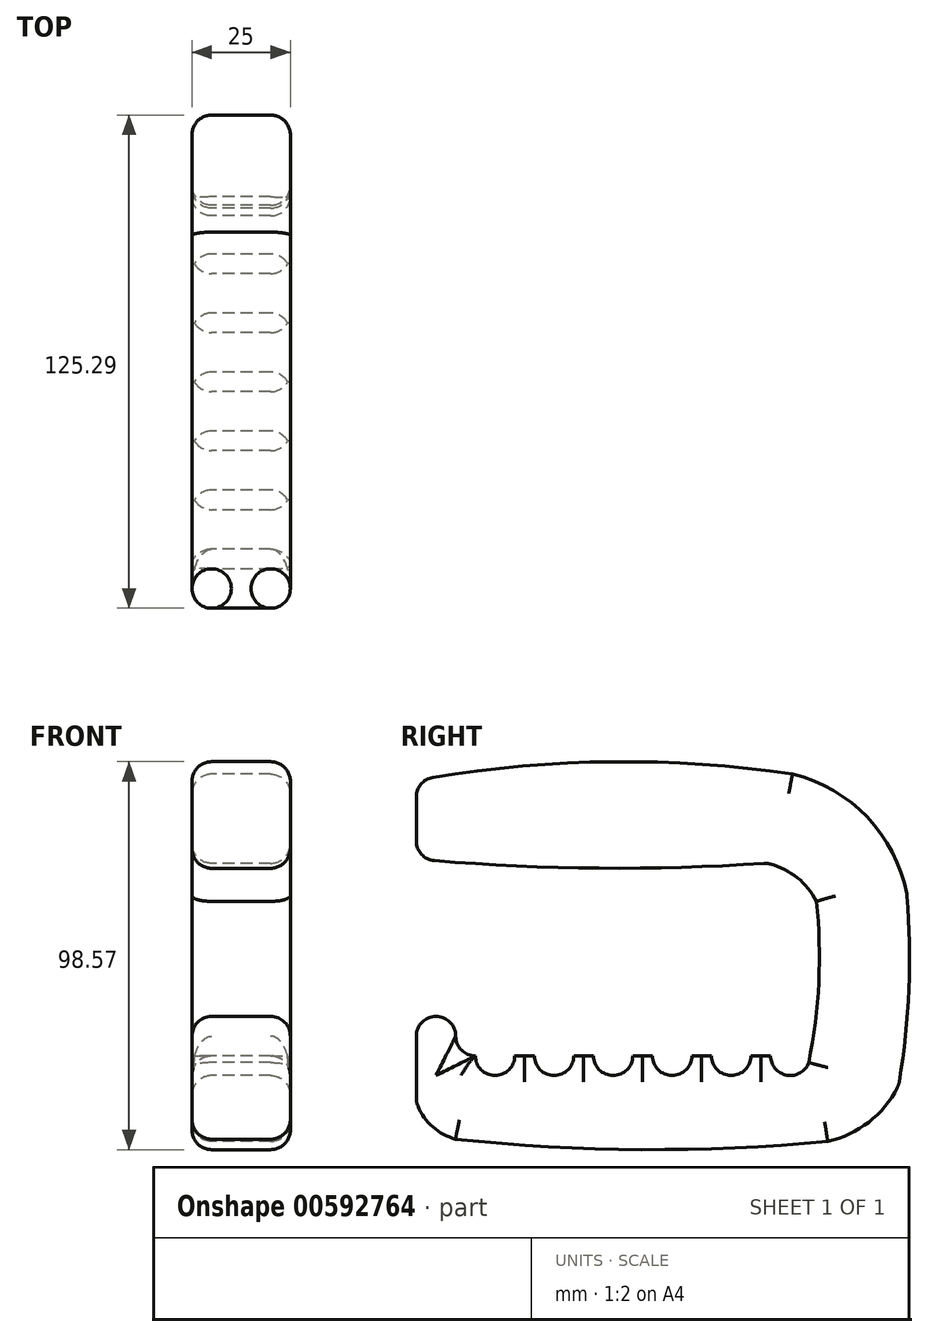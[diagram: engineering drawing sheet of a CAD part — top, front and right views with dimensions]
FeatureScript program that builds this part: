
annotation { "Feature Type Name" : "Feature", "Feature Type Description" : "" }
export const myFeature = defineFeature(function(context is Context, id is Id, definition is map)
    precondition{}
    {
        {
            var Q0;
            Q0=qCreatedBy(makeId("Right.planeOp"),FACE);
            var sketch = newSketch(context, id + "F0", { "sketchPlane" : qUnion([Q0])});
            skLineSegment(sketch, "E0", {"start": v(0, 0) * mm, "end": v(0, 90) * mm, "construction": true});
            skLineSegment(sketch, "E1", {"start": v(-120, 90) * mm, "end": v(-120, 70) * mm});
            skLineSegment(sketch, "E2", {"start": v(-120, 8.28) * mm, "end": v(-120, 30) * mm});
            skLineSegment(sketch, "E3", {"start": v(-120, 30) * mm, "end": v(-110, 30) * mm});
            skLineSegment(sketch, "E4", {"start": v(-110, 30) * mm, "end": v(-110, 20) * mm});
            skPoint(sketch, "E5.orphan", {"position": v(-120, 20) * mm});
            skLineSegment(sketch, "E6", {"start": v(-110, 20) * mm, "end": v(-105, 20) * mm});
            skArc(sketch, "E7", {"start": v(-105, 20) * mm, "mid": v(-100, 15) * mm, "end": v(-95, 20) * mm});
            skLineSegment(sketch, "E8", {"start": v(-95, 20) * mm, "end": v(-90, 20) * mm});
            skArc(sketch, "E9", {"start": v(-90, 20) * mm, "mid": v(-85, 15) * mm, "end": v(-80, 20) * mm});
            skLineSegment(sketch, "E10", {"start": v(-80, 20) * mm, "end": v(-75, 20) * mm});
            skArc(sketch, "E11", {"start": v(-75, 20) * mm, "mid": v(-70, 15) * mm, "end": v(-65, 20) * mm});
            skLineSegment(sketch, "E12", {"start": v(-65, 20) * mm, "end": v(-60, 20) * mm});
            skArc(sketch, "E13", {"start": v(-60, 20) * mm, "mid": v(-55, 15) * mm, "end": v(-50, 20) * mm});
            skLineSegment(sketch, "E14", {"start": v(-50, 20) * mm, "end": v(-45, 20) * mm});
            skArc(sketch, "E15", {"start": v(-45, 20) * mm, "mid": v(-40, 15) * mm, "end": v(-35, 20) * mm});
            skLineSegment(sketch, "E16", {"start": v(-35, 20) * mm, "end": v(-30, 20) * mm});
            skArc(sketch, "E17", {"start": v(-30, 20) * mm, "mid": v(-25.86, 15.08) * mm, "end": v(-20.3, 18.3) * mm});
            skArc(sketch, "E18", {"start": v(2.59, 12.74) * mm, "mid": v(5.11, 36.72) * mm, "end": v(4.64, 60.83) * mm});
            skArc(sketch, "E19", {"start": v(-120, 70) * mm, "mid": v(-75.5, 67.7) * mm, "end": v(-30.96, 68.94) * mm});
            skPoint(sketch, "E20.orphan", {"position": v(-17.66, 70) * mm});
            skArc(sketch, "E21", {"start": v(-110.03, -1.17) * mm, "mid": v(-62.77, -3.83) * mm, "end": v(-15.48, -1.73) * mm});
            skArc(sketch, "E22", {"start": v(-20.3, 18.3) * mm, "mid": v(-17.75, 38.7) * mm, "end": v(-18.34, 59.25) * mm});
            skArc(sketch, "E23", {"start": v(-120, 8.28) * mm, "mid": v(-116.22, 2.29) * mm, "end": v(-110.03, -1.17) * mm});
            skArc(sketch, "E24", {"start": v(-18.34, 59.25) * mm, "mid": v(-23.55, 65.52) * mm, "end": v(-30.96, 68.94) * mm});
            skPoint(sketch, "E25.orphan", {"position": v(-120, 0) * mm});
            skArc(sketch, "E26", {"start": v(4.64, 60.83) * mm, "mid": v(-5.31, 80.53) * mm, "end": v(-24.43, 91.57) * mm});
            skArc(sketch, "E27", {"start": v(-15.48, -1.73) * mm, "mid": v(-4.75, 3.39) * mm, "end": v(2.59, 12.74) * mm});
            skArc(sketch, "E28", {"start": v(-24.43, 91.57) * mm, "mid": v(-72.28, 94.7) * mm, "end": v(-120, 90) * mm});
            skSolve(sketch);
        }
        {
            var Q0;
            Q0 = qSketchRegion(id + "F0", true);
            extrude(context, id + "F1", {"entities" : qUnion([Q0]), "depth" : 25 * mm, "offsetDistance" : 25 * mm});
        }
        {
            var Q0;
            Q0=makeQuery(id+"F1.opExtrude","SWEPT_EDGE",EDGE,{"disambiguationData":[OSD([sQuery(id+"F0.wireOp",EDGE,"gFbuTpBh-fAw6-cQjI-DHgM-E3VqFJ8xNRID"),sQuery(id+"F0.wireOp",EDGE,"E19")])]});
            fillet(context, id + "F2", {"entities" : qUnion([Q0]), "radius" : 5 * mm, "tangentPropagation" : true, "allowEdgeOverflow" : false});
        }
        {
            var Q0;
            Q0=makeQuery(id+"F1.opExtrude","CAP_FACE",FACE,{"disambiguationData":[OSD([sQuery(id+"F0.wireOp",EDGE,"01j4fs1R-nS5N-qxnK-bm29-oMVmBZFqEqTy"),sQuery(id+"F0.wireOp",EDGE,"E1"),sQuery(id+"F0.wireOp",EDGE,"E2"),sQuery(id+"F0.wireOp",EDGE,"E3"),sQuery(id+"F0.wireOp",EDGE,"E4"),sQuery(id+"F0.wireOp",EDGE,"E6"),sQuery(id+"F0.wireOp",EDGE,"E7"),sQuery(id+"F0.wireOp",EDGE,"E8"),sQuery(id+"F0.wireOp",EDGE,"E9"),sQuery(id+"F0.wireOp",EDGE,"E10"),sQuery(id+"F0.wireOp",EDGE,"E11"),sQuery(id+"F0.wireOp",EDGE,"E12"),sQuery(id+"F0.wireOp",EDGE,"E13"),sQuery(id+"F0.wireOp",EDGE,"E14"),sQuery(id+"F0.wireOp",EDGE,"E15"),sQuery(id+"F0.wireOp",EDGE,"E16"),sQuery(id+"F0.wireOp",EDGE,"E17"),sQuery(id+"F0.wireOp",EDGE,"E18"),sQuery(id+"F0.wireOp",EDGE,"gFbuTpBh-fAw6-cQjI-DHgM-E3VqFJ8xNRID"),sQuery(id+"F0.wireOp",EDGE,"2r3oXNqc-cFRX-ebGc-EHzO-GiPthvR7Yf0G"),sQuery(id+"F0.wireOp",EDGE,"E19")])],"isStart":true});
            var Q1;
            Q1=makeQuery(id+"F1.opExtrude","CAP_FACE",FACE,{"disambiguationData":[OSD([sQuery(id+"F0.wireOp",EDGE,"01j4fs1R-nS5N-qxnK-bm29-oMVmBZFqEqTy"),sQuery(id+"F0.wireOp",EDGE,"E1"),sQuery(id+"F0.wireOp",EDGE,"E2"),sQuery(id+"F0.wireOp",EDGE,"E3"),sQuery(id+"F0.wireOp",EDGE,"E4"),sQuery(id+"F0.wireOp",EDGE,"E6"),sQuery(id+"F0.wireOp",EDGE,"E7"),sQuery(id+"F0.wireOp",EDGE,"E8"),sQuery(id+"F0.wireOp",EDGE,"E9"),sQuery(id+"F0.wireOp",EDGE,"E10"),sQuery(id+"F0.wireOp",EDGE,"E11"),sQuery(id+"F0.wireOp",EDGE,"E12"),sQuery(id+"F0.wireOp",EDGE,"E13"),sQuery(id+"F0.wireOp",EDGE,"E14"),sQuery(id+"F0.wireOp",EDGE,"E15"),sQuery(id+"F0.wireOp",EDGE,"E16"),sQuery(id+"F0.wireOp",EDGE,"E17"),sQuery(id+"F0.wireOp",EDGE,"E18"),sQuery(id+"F0.wireOp",EDGE,"gFbuTpBh-fAw6-cQjI-DHgM-E3VqFJ8xNRID"),sQuery(id+"F0.wireOp",EDGE,"2r3oXNqc-cFRX-ebGc-EHzO-GiPthvR7Yf0G"),sQuery(id+"F0.wireOp",EDGE,"E19")])],"isStart":false});
            var Q2;
            Q2=makeQuery(id+"F1.opExtrude","SWEPT_EDGE",EDGE,{"disambiguationData":[OSD([sQuery(id+"F0.wireOp",EDGE,"E18"),sQuery(id+"F0.wireOp",EDGE,"2r3oXNqc-cFRX-ebGc-EHzO-GiPthvR7Yf0G")])]});
            var Q3;
            Q3=makeQuery(id+"F1.opExtrude","SWEPT_EDGE",EDGE,{"disambiguationData":[OSD([sQuery(id+"F0.wireOp",EDGE,"E1"),sQuery(id+"F0.wireOp",EDGE,"2r3oXNqc-cFRX-ebGc-EHzO-GiPthvR7Yf0G")])]});
            var Q4;
            Q4=makeQuery(id+"F1.opExtrude","SWEPT_EDGE",EDGE,{"disambiguationData":[OSD([sQuery(id+"F0.wireOp",EDGE,"01j4fs1R-nS5N-qxnK-bm29-oMVmBZFqEqTy"),sQuery(id+"F0.wireOp",EDGE,"E18")])]});
            var Q5;
            Q5=makeQuery(id+"F1.opExtrude","SWEPT_EDGE",EDGE,{"disambiguationData":[OSD([sQuery(id+"F0.wireOp",EDGE,"01j4fs1R-nS5N-qxnK-bm29-oMVmBZFqEqTy"),sQuery(id+"F0.wireOp",EDGE,"E2")])]});
            var Q6;
            Q6=makeQuery(id+"F1.opExtrude","SWEPT_EDGE",EDGE,{"disambiguationData":[OSD([sQuery(id+"F0.wireOp",EDGE,"E2"),sQuery(id+"F0.wireOp",EDGE,"E3")])]});
            var Q7;
            Q7=makeQuery(id+"F1.opExtrude","SWEPT_EDGE",EDGE,{"disambiguationData":[OSD([sQuery(id+"F0.wireOp",EDGE,"E3"),sQuery(id+"F0.wireOp",EDGE,"E4")])]});
            fillet(context, id + "F3", {"entities" : qUnion([Q0, Q1, Q2, Q3, Q4, Q5, Q6, Q7]), "radius" : 5 * mm, "tangentPropagation" : true, "allowEdgeOverflow" : false});
        }
        {
            var Q0;
            Q0=makeQuery(id+"F1.opExtrude","SWEPT_EDGE",EDGE,{"disambiguationData":[OSD([sQuery(id+"F0.wireOp",EDGE,"E4"),sQuery(id+"F0.wireOp",EDGE,"E6")])]});
            fillet(context, id + "F4", {"entities" : qUnion([Q0]), "radius" : 5 * mm, "tangentPropagation" : true, "allowEdgeOverflow" : false});
        }
    });
